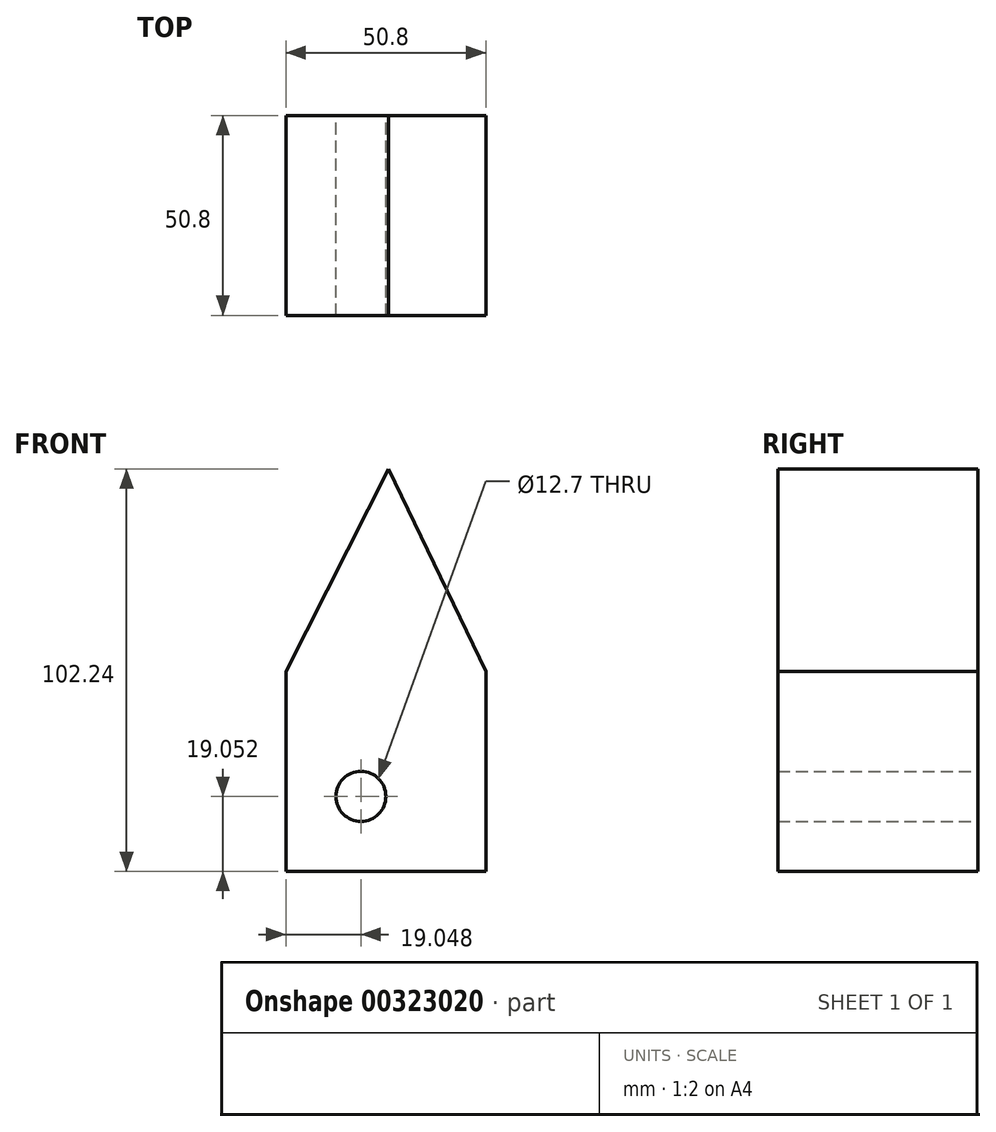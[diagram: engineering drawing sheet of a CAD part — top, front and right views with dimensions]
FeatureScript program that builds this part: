
annotation { "Feature Type Name" : "Feature", "Feature Type Description" : "" }
export const myFeature = defineFeature(function(context is Context, id is Id, definition is map)
    precondition{}
    {
        {
            var Q0;
            Q0=qCreatedBy(makeId("Front.planeOp"),FACE);
            var sketch = newSketch(context, id + "F0", { "sketchPlane" : qUnion([Q0])});
            skLineSegment(sketch, "E0.top", {"start": v(-26.04, -25.32) * mm, "end": v(24.76, -25.32) * mm});
            skLineSegment(sketch, "E0.left", {"start": v(-26.04, 25.48) * mm, "end": v(-26.04, -25.32) * mm});
            skLineSegment(sketch, "E0.right", {"start": v(24.76, 25.48) * mm, "end": v(24.76, -25.32) * mm});
            skLineSegment(sketch, "E1", {"start": v(-26.04, 25.48) * mm, "end": v(0, 76.92) * mm});
            skLineSegment(sketch, "E2", {"start": v(0, 76.92) * mm, "end": v(-26.04, 25.48) * mm});
            skLineSegment(sketch, "E3", {"start": v(0, 76.92) * mm, "end": v(24.76, 25.48) * mm});
            skLineSegment(sketch, "E4.0", {"start": v(-45.32, 99.87) * mm, "end": v(-71.36, 48.43) * mm});
            skLineSegment(sketch, "E5.0", {"start": v(45.77, 98.95) * mm, "end": v(70.53, 47.51) * mm});
            skCircle(sketch, "E6", {"center": v(-7, -6.27) * mm, "radius": 6.35 * mm});
            skSolve(sketch);
        }
        {
            var Q0;
            Q0 = qSketchRegion(id + "F0", true);
            extrude(context, id + "F1", {"entities" : qUnion([Q0]), "depth" : 50.8 * mm});
        }
    });
